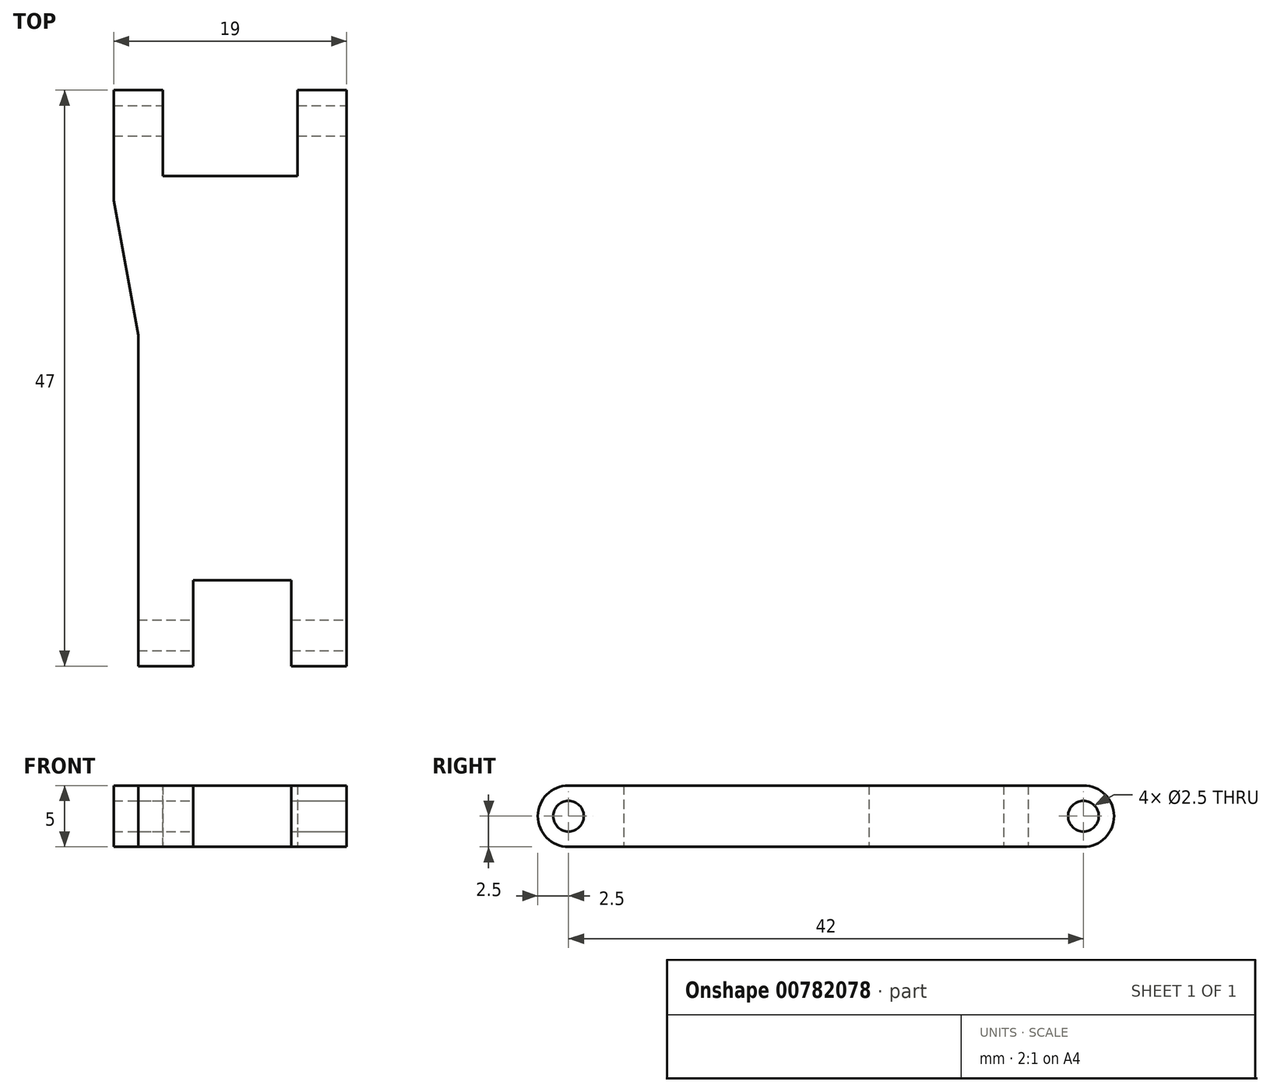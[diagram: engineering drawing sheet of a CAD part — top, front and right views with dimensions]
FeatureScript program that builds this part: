
annotation { "Feature Type Name" : "Feature", "Feature Type Description" : "" }
export const myFeature = defineFeature(function(context is Context, id is Id, definition is map)
    precondition{}
    {
        {
            var Q0;
            Q0=qCreatedBy(makeId("Top.planeOp"),FACE);
            var sketch = newSketch(context, id + "F0", { "sketchPlane" : qUnion([Q0])});
            skLineSegment(sketch, "E0", {"start": v(-8.5, 0) * mm, "end": v(-4, 0) * mm});
            skLineSegment(sketch, "E1", {"start": v(8.5, 0) * mm, "end": v(8.5, 47) * mm});
            skLineSegment(sketch, "E2", {"start": v(8.5, 47) * mm, "end": v(4.5, 47) * mm});
            skLineSegment(sketch, "E3", {"start": v(-4, 0) * mm, "end": v(-4, 7) * mm});
            skLineSegment(sketch, "E4", {"start": v(-4, 7) * mm, "end": v(4, 7) * mm});
            skLineSegment(sketch, "E5", {"start": v(4, 7) * mm, "end": v(4, 0) * mm});
            skLineSegment(sketch, "E6.trimOffspring", {"start": v(4, 0) * mm, "end": v(8.5, 0) * mm});
            skLineSegment(sketch, "E7", {"start": v(0, 0) * mm, "end": v(0, 7) * mm, "construction": true});
            skLineSegment(sketch, "E8", {"start": v(-8.5, 0) * mm, "end": v(-8.5, 27) * mm});
            skLineSegment(sketch, "E9", {"start": v(-10.5, 47) * mm, "end": v(-10.5, 38) * mm});
            skLineSegment(sketch, "E10", {"start": v(-10.5, 38) * mm, "end": v(-8.5, 27) * mm});
            skLineSegment(sketch, "E11", {"start": v(-6.5, 47) * mm, "end": v(-6.5, 40) * mm});
            skLineSegment(sketch, "E12", {"start": v(-6.5, 40) * mm, "end": v(4.5, 40) * mm});
            skLineSegment(sketch, "E13", {"start": v(4.5, 40) * mm, "end": v(4.5, 47) * mm});
            skLineSegment(sketch, "E14.trimOffspring", {"start": v(-6.5, 47) * mm, "end": v(-10.5, 47) * mm});
            skSolve(sketch);
        }
        {
            var Q0;
            Q0=qSketchRegion(id+"F0",true);
            extrude(context, id + "F1", {"entities" : qUnion([Q0]), "depth" : 5 * mm, "symmetric" : true});
        }
        {
            var Q0;
            Q0=qCreatedBy(makeId("Right.planeOp"),FACE);
            var sketch = newSketch(context, id + "F2", { "sketchPlane" : qUnion([Q0])});
            skCircle(sketch, "E15", {"center": v(2.5, 0) * mm, "radius": 1.25 * mm});
            skArc(sketch, "E16", {"start": v(2.5, 2.5) * mm, "mid": v(0, 0) * mm, "end": v(2.5, -2.5) * mm});
            skCircle(sketch, "E17", {"center": v(44.5, 0) * mm, "radius": 1.25 * mm});
            skArc(sketch, "E18", {"start": v(44.5, -2.5) * mm, "mid": v(47, 0) * mm, "end": v(44.5, 2.5) * mm});
            skLineSegment(sketch, "E19", {"start": v(2.5, 2.5) * mm, "end": v(0, 2.5) * mm});
            skLineSegment(sketch, "E20", {"start": v(0, 2.5) * mm, "end": v(0, -2.5) * mm});
            skLineSegment(sketch, "E21", {"start": v(0, -2.5) * mm, "end": v(2.5, -2.5) * mm});
            skLineSegment(sketch, "E22", {"start": v(44.5, 2.5) * mm, "end": v(47, 2.5) * mm});
            skLineSegment(sketch, "E23", {"start": v(47, 2.5) * mm, "end": v(47, -2.5) * mm});
            skLineSegment(sketch, "E24", {"start": v(47, -2.5) * mm, "end": v(44.5, -2.5) * mm});
            skSolve(sketch);
        }
        {
            var Q0;
            Q0=qSketchRegion(id+"F2",true);
            extrude(context, id + "F3", {"entities" : qUnion([Q0]), "operationType" : NewBodyOperationType.REMOVE, "endBound" : BoundingType.THROUGH_ALL, "oppositeDirection" : true, "depth" : 25 * mm, "hasSecondDirection" : true, "secondDirectionBound" : BoundingType.THROUGH_ALL, "secondDirectionOppositeDirection" : false, "secondDirectionDepth" : 25 * mm});
        }
    });
